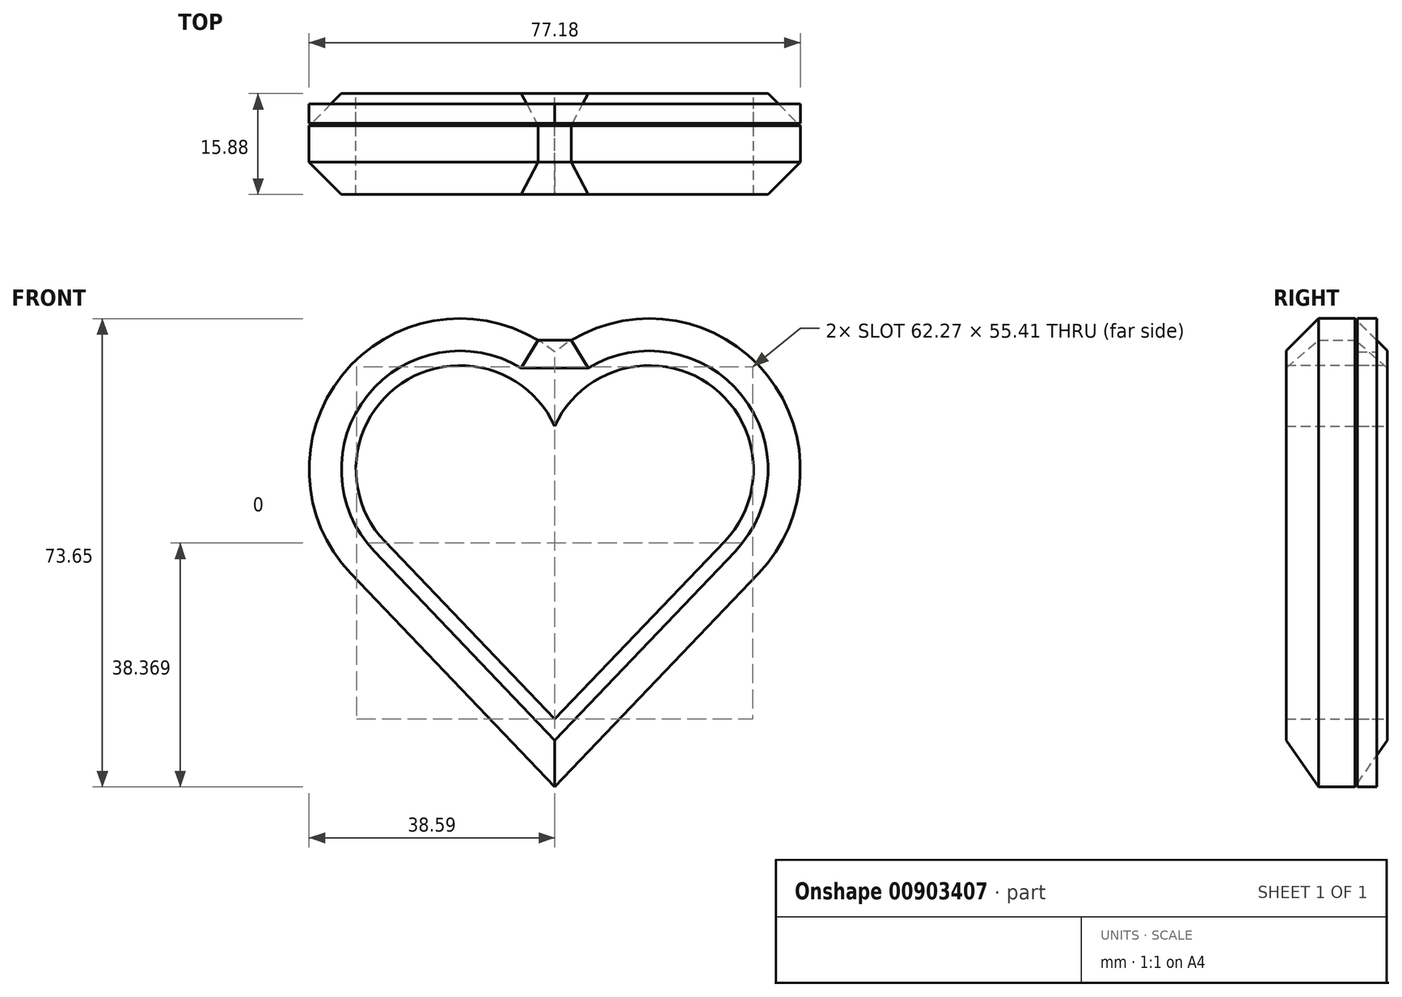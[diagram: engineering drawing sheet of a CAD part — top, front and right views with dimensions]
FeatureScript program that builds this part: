
annotation { "Feature Type Name" : "Feature", "Feature Type Description" : "" }
export const myFeature = defineFeature(function(context is Context, id is Id, definition is map)
    precondition{}
    {
        {
            var Q0;
            Q0=qCreatedBy(makeId("Front.planeOp"),FACE);
            var sketch = newSketch(context, id + "F0", { "sketchPlane" : qUnion([Q0])});
            skLineSegment(sketch, "E0", {"start": v(0, 0) * mm, "end": v(32.03, 33.54) * mm});
            skArc(sketch, "E1", {"start": v(32.03, 33.54) * mm, "mid": v(32.34, 65.98) * mm, "end": v(0, 68.42) * mm});
            skArc(sketch, "E2.MirrorCS", {"start": v(-32.03, 33.54) * mm, "mid": v(-32.34, 65.98) * mm, "end": v(0, 68.42) * mm});
            skLineSegment(sketch, "E3.MirrorCS", {"start": v(0, 0) * mm, "end": v(-32.03, 33.54) * mm});
            skArc(sketch, "E4.0", {"start": v(-26.7, 38.63) * mm, "mid": v(-24.06, 63.46) * mm, "end": v(0, 56.75) * mm});
            skLineSegment(sketch, "E4.1", {"start": v(0, 10.67) * mm, "end": v(-26.7, 38.63) * mm});
            skLineSegment(sketch, "E4.2", {"start": v(0, 10.67) * mm, "end": v(26.7, 38.63) * mm});
            skArc(sketch, "E4.3", {"start": v(26.7, 38.63) * mm, "mid": v(24.06, 63.46) * mm, "end": v(0, 56.75) * mm});
            skSolve(sketch);
        }
        {
            var Q0;
            Q0=makeQuery(id+"F0.imprint","IMPRINT",FACE,{"disambiguationData":[TD([[makeQuery(id+"F0.imprint","IMPRINT",EDGE,{"derivedFrom":sQuery(id+"F0.wireOp",EDGE,"E0")}),1.0]])]});
            extrude(context, id + "F1", {"entities" : qUnion([Q0]), "endBound" : BoundingType.SYMMETRIC, "depth" : 6.35 * mm, "offsetDistance" : 25.4 * mm});
        }
        {
            var Q0;
            Q0=makeQuery(id+"F0.imprint","IMPRINT",FACE,{"disambiguationData":[TD([[makeQuery(id+"F0.imprint","IMPRINT",EDGE,{"derivedFrom":sQuery(id+"F0.wireOp",EDGE,"E0")}),1.0]])]});
            extrude(context, id + "F2", {"entities" : qUnion([Q0]), "operationType" : NewBodyOperationType.ADD, "depth" : 12.7 * mm, "offsetDistance" : 25.4 * mm});
        }
        {
            var Q0;
            Q0=makeQuery(id+"F0.imprint","IMPRINT",FACE,{"disambiguationData":[TD([[makeQuery(id+"F0.imprint","IMPRINT",EDGE,{"derivedFrom":sQuery(id+"F0.wireOp",EDGE,"E4.0")}),-1.0]])]});
            extrude(context, id + "F3", {"entities" : qUnion([Q0]), "endBound" : BoundingType.SYMMETRIC, "depth" : 3.05 * mm, "offsetDistance" : 25.4 * mm});
        }
        {
            var Q0;
            Q0=makeQuery(id+"F2.opExtrude","CAP_EDGE",EDGE,{"disambiguationData":[OSD([sQuery(id+"F0.wireOp",EDGE,"E2.MirrorCS")])],"isStart":false});
            var Q1;
            Q1=makeQuery(id+"F2.opExtrude","CAP_EDGE",EDGE,{"disambiguationData":[OSD([sQuery(id+"F0.wireOp",EDGE,"E0")])],"isStart":false});
            var Q2;
            {var subQ0=sQuery(id+"F0.wireOp",EDGE,"E2.MirrorCS");Q2=makeQuery(id+"F2.boolean.opBoolean","MERGE",FACE,{"derivedFrom":[makeQuery(id+"F1.opExtrude","SWEPT_FACE",FACE,{"disambiguationData":[OSD([subQ0])]}),makeQuery(id+"F2.opExtrude","SWEPT_FACE",FACE,{"disambiguationData":[OSD([subQ0])]})]});}
            chamfer(context, id + "F4", {"entities" : qUnion([Q0, Q1, Q2]), "width" : 5.08 * mm, "tangentPropagation" : true});
        }
    });
